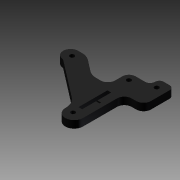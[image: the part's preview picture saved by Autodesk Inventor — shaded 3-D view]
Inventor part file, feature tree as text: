
AUTODESK INVENTOR PART (.ipt)
format: ipt  version: 2012 (Build 160160000, 160)  size: 133,632 bytes
history: native  units: mm
features: extrude x1, sketch x1
ambient origin geometry x8: Origin, YZ Plane, XZ Plane, XY Plane, X Axis, Y Axis, Z Axis, Center Point
bodies: Solid1 (feature_tree)
feature tree (2):
  extrude  "Extrusion1"  Depth=1.25mm
  sketch  "Sketch1"  dims[d8=19.85mm d13=1.25mm d15=2.5mm d16=19.8mm d17=5.0mm d20=1.25mm d25=9.4mm d26=2.5mm d27=1.0mm d70=5.0mm d71=5.0mm d72=10.0mm d79=10.0mm d80=5.0mm d83=3.0mm d85=3.0mm d86=5.0mm d87=0.0mm]
